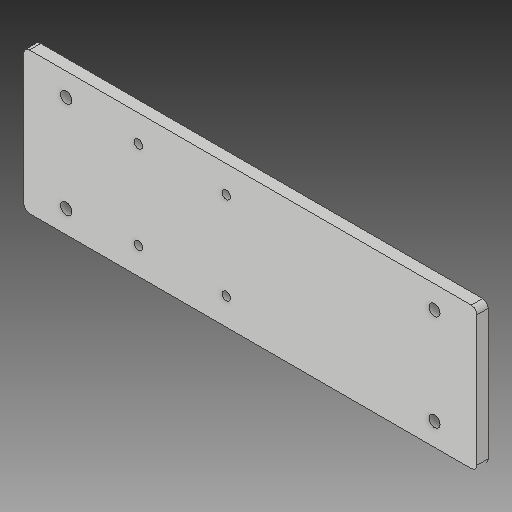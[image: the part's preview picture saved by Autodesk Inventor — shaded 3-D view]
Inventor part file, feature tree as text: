
AUTODESK INVENTOR PART (.ipt)
format: ipt  version: 2019 (Build 230136000, 136)  size: 126,976 bytes
history: native  units: in
note: dims shown in document units (in); Inventor stores cm internally (conversion verified against a paired STEP export)
features: reference x7, other x4, extrude x2, sketch x2, fillet x1, helix x1
ambient origin geometry x8: Origin, YZ Plane, XZ Plane, XY Plane, X Axis, Y Axis, Z Axis, Center Point
bodies: Solid1 (feature_tree)
feature tree (17):
  extrude  "Extrusion1"  Depth=0.1575in TaperAngle=0.0deg
  fillet  "Fillet1"  Radius=0.0787in
  extrude  "Extrusion2"  Depth=0.1575in
  sketch  "Sketch1"  dims[d0=1.9685in d1=0.1575in d2=0.0in d3=0.0787in]
  reference  "Reference1"
  sketch  "Sketch2"  dims[d4=0.1575in d5=0.1575in d6=0.1181in d7=0.1181in d8=0.1181in d9=0.1181in d10=0.1575in d11=0.1575in d12=0.315in d13=0.315in d14=0.315in d15=0.315in d16=0.1575in d17=0.0in]
  reference  "Reference2"
  reference  "Reference3"
  reference  "Reference4"
  reference  "Reference5"
  reference  "Reference6"
  reference  "Reference7"
  other  "<userpath>\Documents\CAD Files\Helix DLP\Helix DLP.iam"
  helix  "Helix DLP.iam"  [1 undecoded]
  other  "30X30 - T-slot - Aluminium Profile:3"
  other  "30X30 - T-slot - Aluminium Profile:1"
  other  "M1173041- NEMA 17 Screw rod:2"
note: 1 required parameter value undecoded (feature->parameter linkage not recoverable at this tier; creation-order binding heuristic only, values carry confidence <= 0.55)
